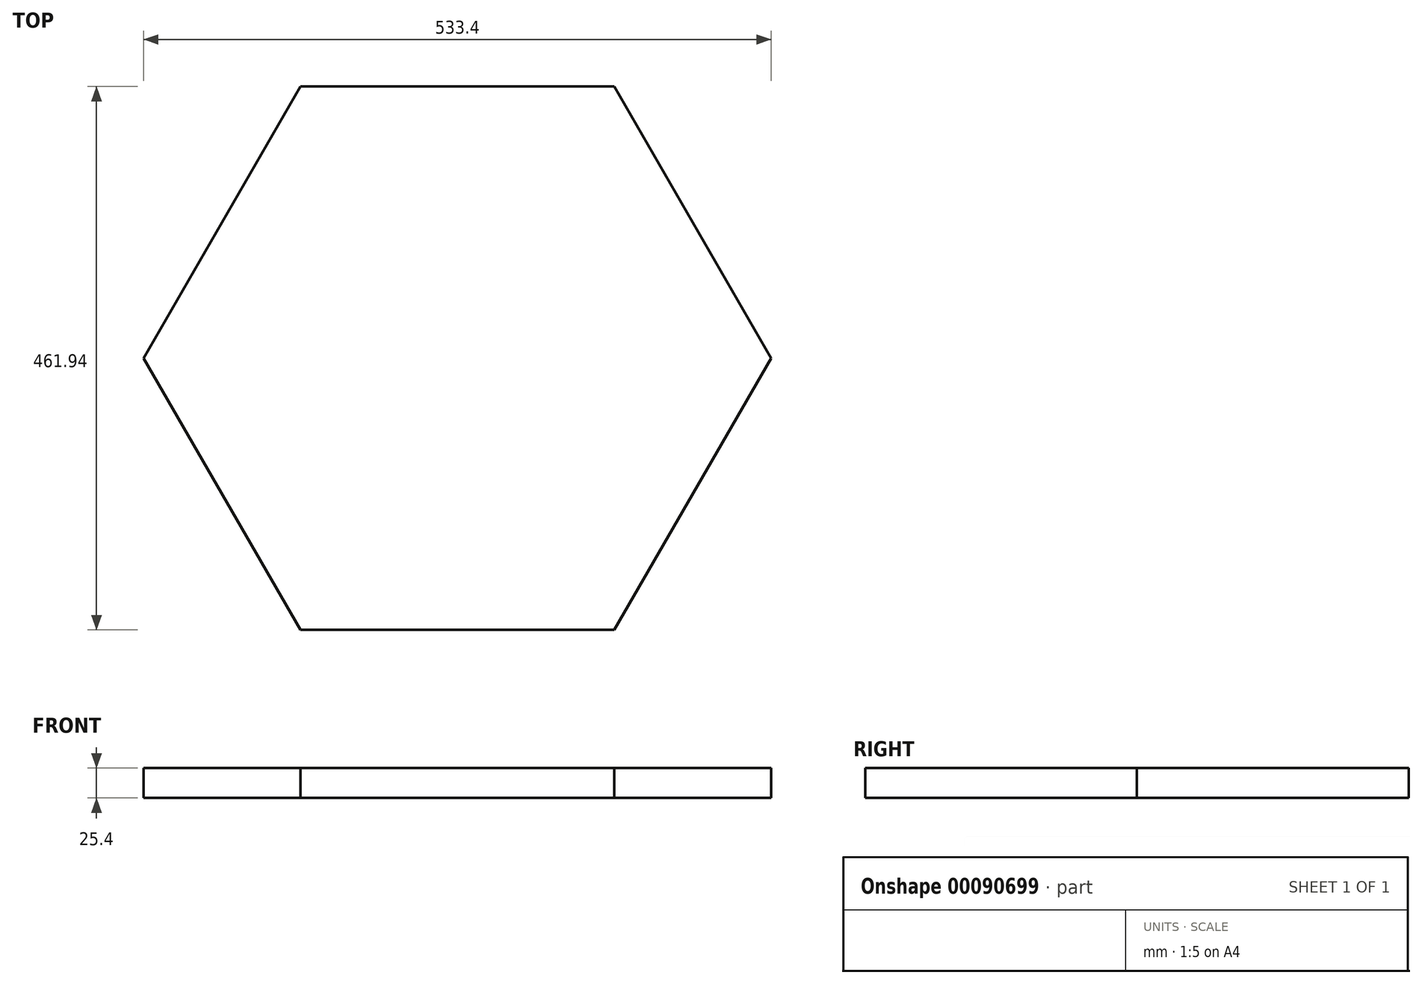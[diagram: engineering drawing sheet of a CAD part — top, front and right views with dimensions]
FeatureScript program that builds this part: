
annotation { "Feature Type Name" : "Feature", "Feature Type Description" : "" }
export const myFeature = defineFeature(function(context is Context, id is Id, definition is map)
    precondition{}
    {
        {
            var Q0;
            Q0=qCreatedBy(makeId("Top.planeOp"),FACE);
            var sketch = newSketch(context, id + "F0", { "sketchPlane" : qUnion([Q0])});
            skCircle(sketch, "E0.cCircle", {"center": v(0, 0) * mm, "radius": 230.97 * mm, "construction": true});
            skLineSegment(sketch, "E0.0", {"start": v(-133.35, 230.97) * mm, "end": v(133.35, 230.97) * mm});
            skLineSegment(sketch, "E0.1", {"start": v(133.35, 230.97) * mm, "end": v(266.7, 0) * mm});
            skLineSegment(sketch, "E0.2", {"start": v(266.7, 0) * mm, "end": v(133.35, -230.97) * mm});
            skLineSegment(sketch, "E0.3", {"start": v(133.35, -230.97) * mm, "end": v(-133.35, -230.97) * mm});
            skLineSegment(sketch, "E0.4", {"start": v(-133.35, -230.97) * mm, "end": v(-266.7, 0) * mm});
            skLineSegment(sketch, "E0.5", {"start": v(-266.7, 0) * mm, "end": v(-133.35, 230.97) * mm});
            skPoint(sketch, "E0.0.midPoint", {"position": v(0, 230.97) * mm});
            skSolve(sketch);
        }
        {
            var Q0;
            Q0=makeQuery(id+"F0.imprint","IMPRINT",FACE,{"disambiguationData":[TD([[makeQuery(id+"F0.imprint","IMPRINT",EDGE,{"derivedFrom":sQuery(id+"F0.wireOp",EDGE,"E0.0")}),-1.0]])]});
            extrude(context, id + "F1", {"entities" : qUnion([Q0]), "depth" : 25.4 * mm});
        }
    });
